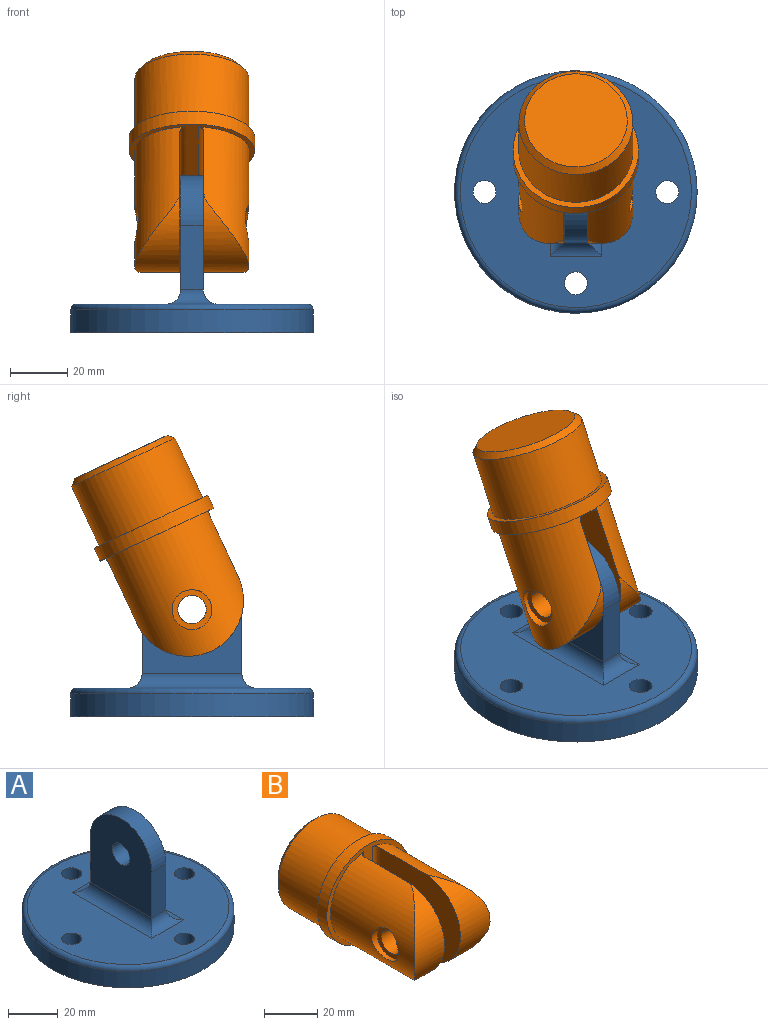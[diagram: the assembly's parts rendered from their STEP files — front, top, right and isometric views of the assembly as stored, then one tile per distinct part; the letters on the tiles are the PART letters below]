
ASSEMBLY  parts=2 mates=1
PART A: 18 faces, bbox 92x92x55 mm
  f0: cylinder r=4mm len=10mm, axis (0,0,1), area 251.3mm2, adj f4,f5
  f1: cylinder r=4mm len=10mm, axis (0,0,1), area 251.3mm2, adj f4,f5
  f2: cylinder r=4mm len=10mm, axis (0,0,1), area 251.3mm2, adj f4,f5
  f3: cylinder r=42.5mm len=85mm, axis (0,0,1), area 2136.3mm2, adj f4,f13
  f4: plane 85x85mm, normal (0,0,-1), area 5473.4mm2, adj f0,f1,f2,f3,f6
  f5: plane 81x81mm, normal (0,0,1), area 4141.9mm2, adj f0,f1,f2,f6,f13,f14,f15,f16
  f6: cylinder r=4mm len=10mm, axis (0,0,1), area 251.3mm2, adj f4,f5
  f7: plane 22.5x8mm, normal (0,1,0), area 180mm2, adj f9,f10,f11,f17
  f8: plane 22.5x8mm, normal (0,-1,0), area 180mm2, adj f9,f10,f11,f14
  f9: plane 40x35mm, normal (1,0,0), area 1190mm2, adj f7,f8,f11,f12,f15
  f10: plane 40x35mm, normal (-1,0,0), area 1190mm2, adj f7,f8,f11,f12,f16
  f11: cylinder r=17.5mm len=35mm, axis (1,0,0), area 439.8mm2, adj f7,f8,f9,f10
  f12: cylinder r=5mm len=10mm, axis (1,0,0), area 251.3mm2, adj f9,f10
  f13: torus R=40.5mm, axis (0,0,1), area 824.6mm2, adj f3,f5
  f14: cylinder r=5mm len=18mm, axis (1,0,0), area 91.4mm2, adj f5,f8,f15,f16
  f15: cylinder r=5mm len=45mm, axis (0,1,0), area 303.4mm2, adj f5,f9,f14,f17
  f16: cylinder r=5mm len=45mm, axis (0,-1,0), area 303.4mm2, adj f5,f10,f14,f17
  f17: cylinder r=5mm len=18mm, axis (-1,0,0), area 91.4mm2, adj f5,f7,f15,f16
PART B: 20 faces, bbox 44x75x44 mm
  f0: cylinder r=20mm len=45mm, axis (0,-1,0), area 1967.6mm2, adj f1,f8,f13,f15,f19
  f1: plane 43x39.11mm, normal (1,0,0), area 1439mm2, adj f0,f13,f15,f17
  f2: plane 43x39.11mm, normal (-1,0,0), area 1439mm2, adj f3,f9,f12,f16
  f3: cylinder r=20mm len=45mm, axis (0,-1,0), area 1967.6mm2, adj f2,f8,f11,f12,f16
  f4: plane 36x36mm, normal (0,1,0), area 1017.9mm2, adj f14
  f5: cylinder r=20mm len=40mm, axis (0,-1,0), area 2890.3mm2, adj f6,f14
  f6: plane 44x44mm, normal (0,1,0), area 263.9mm2, adj f5,f7
  f7: cylinder r=22mm len=44mm, axis (0,-1,0), area 691.2mm2, adj f6,f8
  f8: plane 44x44mm, normal (0,-1,0), area 439.5mm2, adj f0,f3,f7,f15,f16
  f9: cylinder r=5mm len=12.8mm, axis (1,0,0), area 402.1mm2, adj f2,f10
  f10: plane 14x14mm, normal (1,0,0), area 75.4mm2, adj f9,f11
  f11: cylinder r=7mm len=14mm, axis (1,0,0), area 104.4mm2, adj f3,f10
  f12: cylinder r=19.55mm len=39.11mm, axis (-1,0,0), area 567mm2, adj f2,f3
  f13: cylinder r=19.55mm len=39.11mm, axis (-1,0,0), area 566.8mm2, adj f0,f1
  f14: cone r=20mm half-angle=45deg, axis (0,-1,0), area 337.7mm2, adj f4,f5
  f15: cylinder r=2mm len=39.76mm, axis (0,0,-1), area 123.7mm2, adj f0,f1,f8
  f16: cylinder r=2mm len=39.76mm, axis (0,0,1), area 123.7mm2, adj f2,f3,f8
  f17: cylinder r=5mm len=12.8mm, axis (-1,0,0), area 402.1mm2, adj f1,f18
  f18: plane 14x14mm, normal (-1,0,0), area 75.4mm2, adj f17,f19
  f19: cylinder r=7mm len=14mm, axis (-1,0,0), area 104.4mm2, adj f0,f18
PLACE A at identity fixed
PLACE B rot(axis=(1,0,0),65deg) t=(0,-6.76,13)mm
MATE cylindrical B.f9 <-> A.f12  axis (1,0,0) through (17,0,27.5)mm
